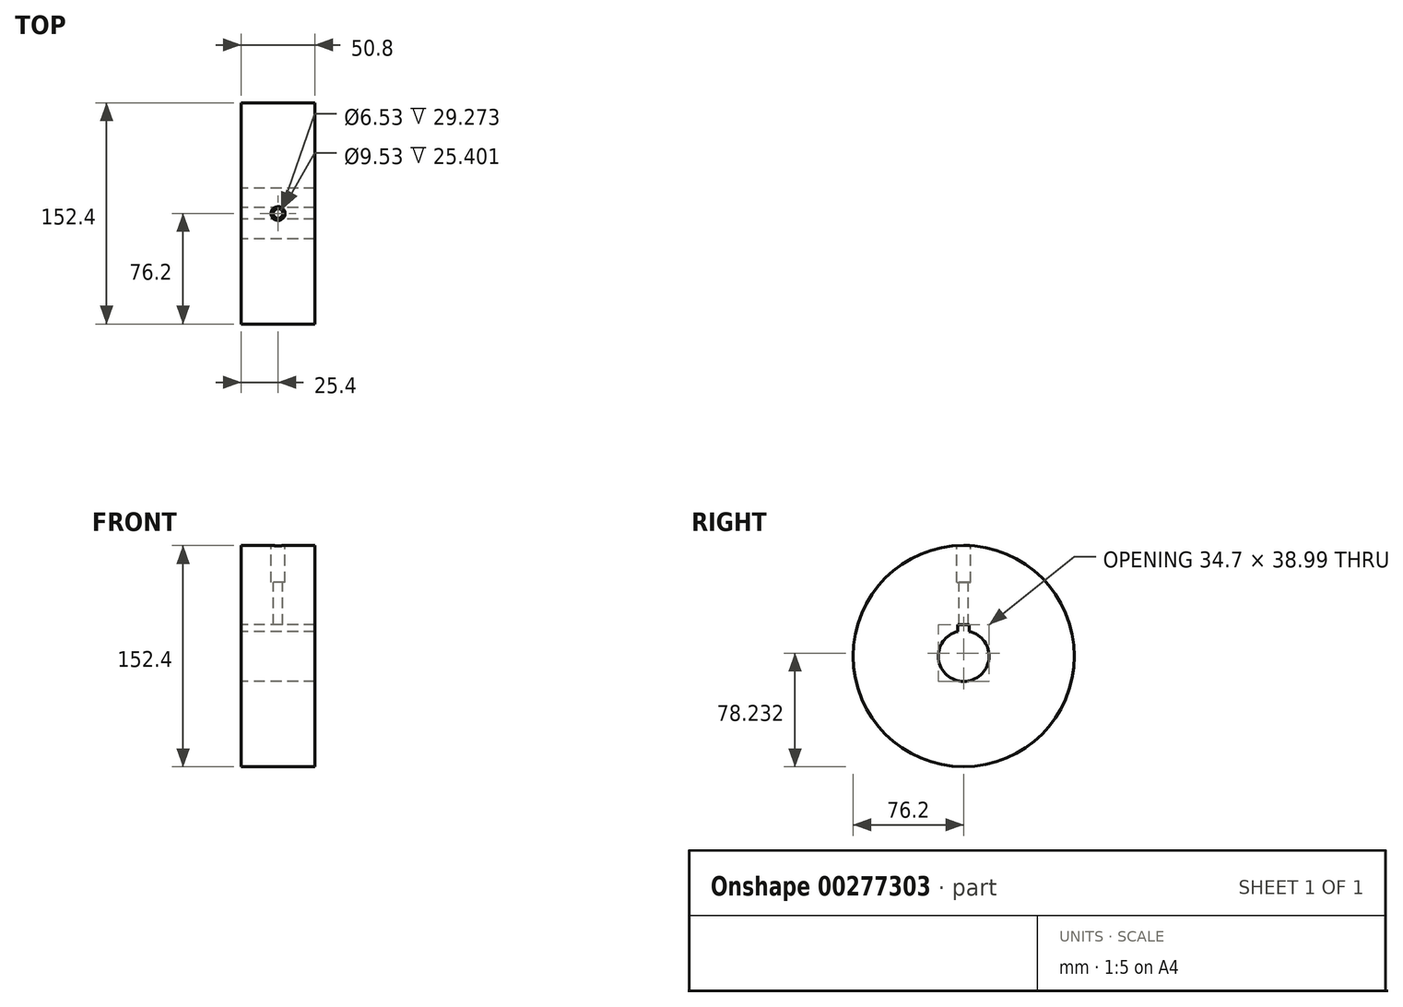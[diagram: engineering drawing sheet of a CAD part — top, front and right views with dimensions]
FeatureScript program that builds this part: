
annotation { "Feature Type Name" : "Feature", "Feature Type Description" : "" }
export const myFeature = defineFeature(function(context is Context, id is Id, definition is map)
    precondition{}
    {
        {
            var Q0;
            Q0=qCreatedBy(makeId("Right.planeOp"),FACE);
            var sketch = newSketch(context, id + "F0", { "sketchPlane" : qUnion([Q0])});
            skArc(sketch, "E0", {"start": v(-3.96, 17) * mm, "mid": v(0, -17.46) * mm, "end": v(3.96, 17) * mm});
            skCircle(sketch, "E1", {"center": v(0, 0) * mm, "radius": 76.2 * mm});
            skLineSegment(sketch, "E2", {"start": v(0, 0) * mm, "end": v(0, 22.93) * mm, "construction": true});
            skLineSegment(sketch, "E3.bottom", {"start": v(-3.96, 21.53) * mm, "end": v(3.96, 21.53) * mm});
            skLineSegment(sketch, "E3.left", {"start": v(-3.96, 21.53) * mm, "end": v(-3.96, 17) * mm});
            skLineSegment(sketch, "E3.right", {"start": v(3.96, 21.53) * mm, "end": v(3.96, 17) * mm});
            skPoint(sketch, "E3.middle", {"position": v(0, 17.46) * mm});
            skPoint(sketch, "E4.orphan", {"position": v(-3.96, 13.4) * mm});
            skPoint(sketch, "E3.top.end.orphan", {"position": v(3.96, 13.4) * mm});
            skSolve(sketch);
        }
        {
            var Q0;
            Q0 = qSketchRegion(id + "F0", true);
            extrude(context, id + "F1", {"entities" : qUnion([Q0]), "endBound" : BoundingType.SYMMETRIC, "depth" : 50.8 * mm});
        }
        {
            var Q0;
            Q0=qCreatedBy(makeId("Top.planeOp"),FACE);
            cPlane(context, id + "F2", {"entities" : qUnion([Q0]), "cplaneType" : CPlaneType.OFFSET, "offset" : 76.2 * mm, "width" : 152.4 * mm, "height" : 152.4 * mm});
        }
        {
            var Q0;
            Q0=qCreatedBy(id+"F2.planeOp",FACE);
            var sketch = newSketch(context, id + "F3", { "sketchPlane" : qUnion([Q0])});
            skPoint(sketch, "E5", {"position": v(0, 0) * mm});
            skSolve(sketch);
        }
        {
            var Q0;
            Q0=sQuery(id+"F3.wireOp",VERTEX,"E5");
            var Q1;
            Q1=makeQuery(id+"F1.opExtrude","SWEPT_BODY",BODY,{"disambiguationData":[OSD([sQuery(id+"F0.wireOp",EDGE,"E0"),sQuery(id+"F0.wireOp",EDGE,"E1"),sQuery(id+"F0.wireOp",EDGE,"E3.bottom"),sQuery(id+"F0.wireOp",EDGE,"E3.left"),sQuery(id+"F0.wireOp",EDGE,"E3.right")])]});
            hole(context, id + "F4", {"style" : HoleStyle.C_BORE, "endStyle" : HoleEndStyle.BLIND, "holeDiameter" : 6.53 * mm, "cBoreDiameter" : 9.52 * mm, "cBoreDepth" : 25.4 * mm, "holeDepth" : 76.2 * mm, "tappedDepth" : 71.97 * mm, "tapClearance" : 3, "startFromSketch" : true, "locations" : qUnion([Q0]), "scope" : qUnion([Q1])});
        }
    });
